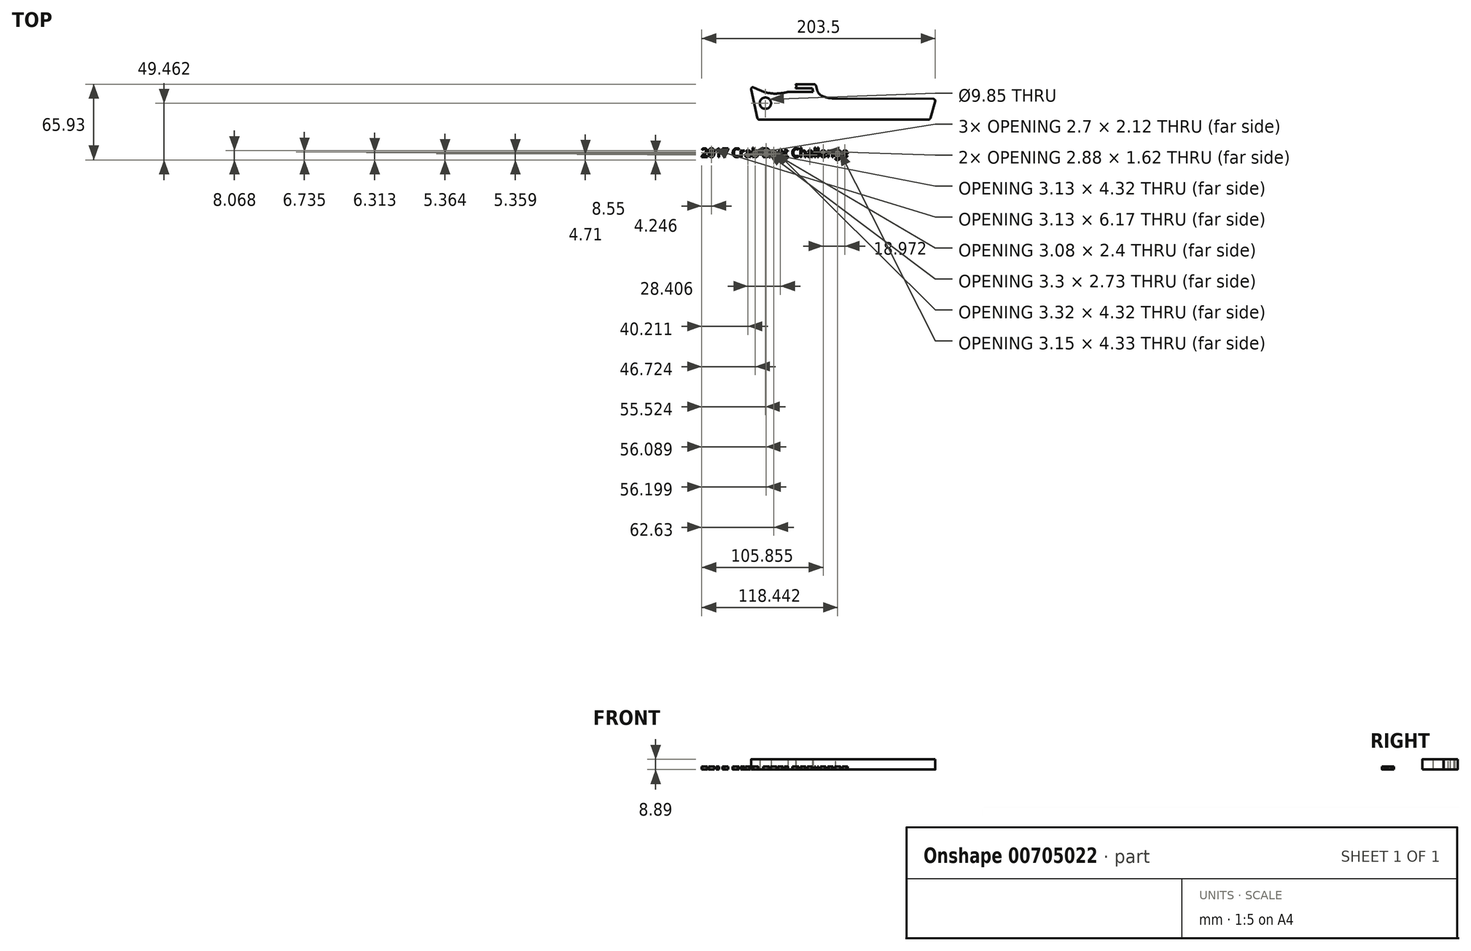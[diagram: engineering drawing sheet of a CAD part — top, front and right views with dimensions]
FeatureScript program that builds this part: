
annotation { "Feature Type Name" : "Feature", "Feature Type Description" : "" }
export const myFeature = defineFeature(function(context is Context, id is Id, definition is map)
    precondition{}
    {
        {
            var Q0;
            Q0=qCreatedBy(makeId("Top.planeOp"),FACE);
            var sketch = newSketch(context, id + "F0", { "sketchPlane" : qUnion([Q0])});
            skLineSegment(sketch, "E0", {"start": v(-84.93, 14.88) * mm, "end": v(-79.38, -10.13) * mm});
            skLineSegment(sketch, "E1", {"start": v(-77.83, -11.38) * mm, "end": v(69.73, -11.38) * mm});
            skLineSegment(sketch, "E2", {"start": v(-29.93, 19.42) * mm, "end": v(-53.77, 19.42) * mm});
            skLineSegment(sketch, "E3", {"start": v(-55.2, 17.15) * mm, "end": v(-54.94, 16.58) * mm});
            skLineSegment(sketch, "E4", {"start": v(-54.94, 16.58) * mm, "end": v(-57.7, 12.86) * mm});
            skLineSegment(sketch, "E5", {"start": v(-57.7, 12.86) * mm, "end": v(-62.45, 12.86) * mm});
            skLineSegment(sketch, "E6", {"start": v(-63.96, 11.78) * mm, "end": v(-64.12, 11.3) * mm});
            skLineSegment(sketch, "E7", {"start": v(-51.47, 16.08) * mm, "end": v(-53.45, 12.85) * mm});
            skLineSegment(sketch, "E8", {"start": v(-53.45, 12.85) * mm, "end": v(-30.76, 12.73) * mm});
            skLineSegment(sketch, "E9", {"start": v(-30.76, 12.73) * mm, "end": v(-31.57, 16.04) * mm});
            skLineSegment(sketch, "E10", {"start": v(-31.57, 16.04) * mm, "end": v(-51.47, 16.08) * mm});
            skLineSegment(sketch, "E11", {"start": v(-12.87, 7.14) * mm, "end": v(73.94, 6.6) * mm});
            skFitSpline(sketch, "E12", {"points": [v(-28.7, 19.42) * mm, v(-24.4, 10.07) * mm, v(-13.1, 10.5) * mm], "startDerivative": vector(6.33, -23.36) * mm, "endDerivative": vector(13.02, 12.63) * mm});
            skFitSpline(sketch, "E13", {"points": [v(-24.4, 10.07) * mm, v(-12.87, 7.14) * mm, v(9.04, 10.07) * mm], "startDerivative": vector(24.02, -14.85) * mm, "endDerivative": vector(42.16, 10.48) * mm});
            skFitSpline(sketch, "E14", {"points": [v(-85.67, 18.21) * mm, v(-64.12, 11.3) * mm, v(-45.47, 17.35) * mm, v(-67.3, 29.92) * mm], "startDerivative": vector(57.78, -30.56) * mm, "endDerivative": vector(-95.71, 37.44) * mm});
            skArc(sketch, "E15.filletArc", {"start": v(-82.66, 16.64) * mm, "mid": v(-84.35, 16.48) * mm, "end": v(-84.93, 14.88) * mm});
            skArc(sketch, "E16.filletArc", {"start": v(-28.39, 18.2) * mm, "mid": v(-28.95, 19.08) * mm, "end": v(-29.93, 19.42) * mm});
            skPoint(sketch, "E17.visualSharp", {"position": v(-79.1, -11.38) * mm});
            skArc(sketch, "E17.filletArc", {"start": v(-79.38, -10.13) * mm, "mid": v(-78.82, -11.03) * mm, "end": v(-77.83, -11.38) * mm});
            skPoint(sketch, "E18.visualSharp", {"position": v(-63.6, 12.86) * mm});
            skArc(sketch, "E18.filletArc", {"start": v(-62.45, 12.86) * mm, "mid": v(-63.38, 12.56) * mm, "end": v(-63.96, 11.78) * mm});
            skPoint(sketch, "E19.visualSharp", {"position": v(-56.29, 19.42) * mm});
            skArc(sketch, "E19.filletArc", {"start": v(-53.77, 19.42) * mm, "mid": v(-55.12, 18.68) * mm, "end": v(-55.2, 17.15) * mm});
            skLineSegment(sketch, "E20", {"start": v(71.25, -10.22) * mm, "end": v(75.46, 4.58) * mm});
            skPoint(sketch, "E21.visualSharp", {"position": v(76.03, 6.58) * mm});
            skArc(sketch, "E21.filletArc", {"start": v(75.46, 4.58) * mm, "mid": v(75.2, 5.96) * mm, "end": v(73.94, 6.6) * mm});
            skPoint(sketch, "E22.visualSharp", {"position": v(70.93, -11.38) * mm});
            skArc(sketch, "E22.filletArc", {"start": v(69.73, -11.38) * mm, "mid": v(70.68, -11.06) * mm, "end": v(71.25, -10.22) * mm});
            skCircle(sketch, "E23", {"center": v(-72.46, 2.95) * mm, "radius": 4.93 * mm});
            skSolve(sketch);
        }
        {
            var Q0;
            Q0=qCreatedBy(makeId("Top.planeOp"),FACE);
            var sketch = newSketch(context, id + "F1", { "sketchPlane" : qUnion([Q0])});
            skText(sketch, "E24", { "text": "2017 Crab Boat Challenge", "fontName": "NotoSans-Regular.ttf"});
            const initialGuessF1  = {"E24": [-0.12848, -0.04397, 1, 0, 0.0076]};
            skSetInitialGuess(sketch, initialGuessF1);
            skSolve(sketch);
        }
        {
            var Q0;
            Q0=makeQuery(id+"F0.imprint","IMPRINT",FACE,{"disambiguationData":[TD([[makeQuery(id+"F0.imprint","IMPRINT",EDGE,{"derivedFrom":sQuery(id+"F0.wireOp",EDGE,"E0")}),1.0]])]});
            extrude(context, id + "F2", {"entities" : qUnion([Q0]), "depth" : 8.9 * mm, "offsetDistance" : 25.4 * mm});
        }
        {
            var Q0;
            Q0 = qSketchRegion(id + "F1", true);
            extrude(context, id + "F3", {"entities" : qUnion([Q0]), "depth" : 2.54 * mm, "offsetDistance" : 25.4 * mm});
        }
    });
